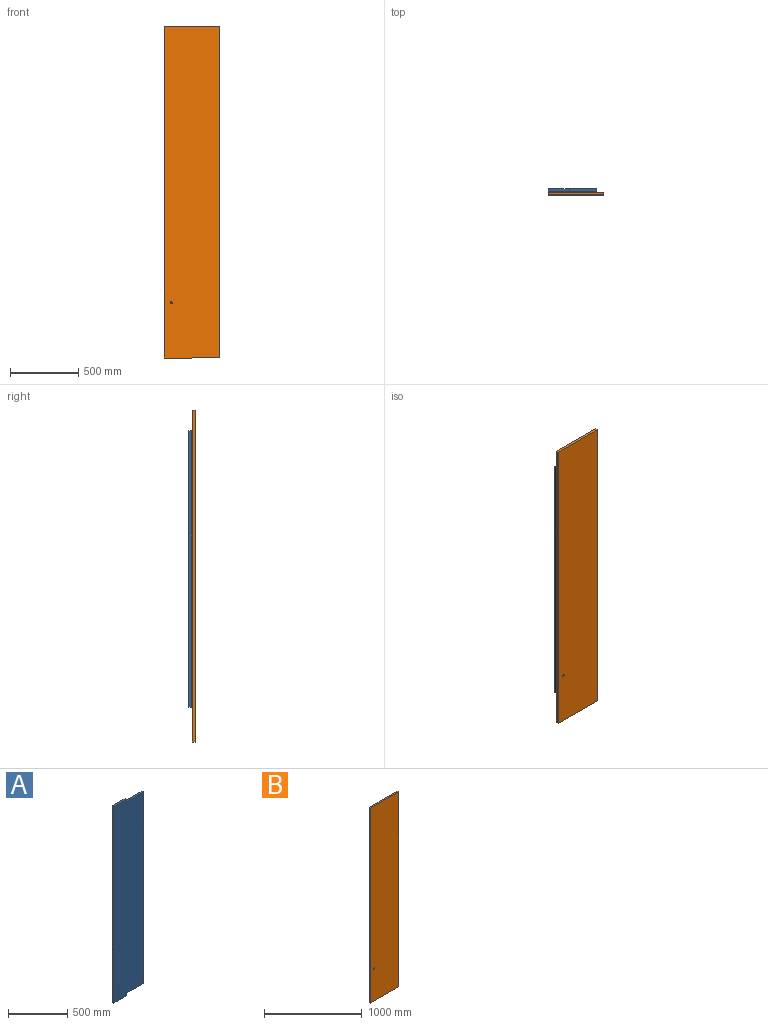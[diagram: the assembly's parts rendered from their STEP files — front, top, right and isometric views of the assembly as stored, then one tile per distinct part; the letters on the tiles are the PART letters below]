
ASSEMBLY  parts=2 mates=1
PART A: 11 faces, bbox 355.6x19.1x2032 mm
  f0: plane 26.04x19.05mm, normal (1,0,0), area 496mm2, adj f1,f7,f9,f10
  f1: plane 203.2x19.05mm, normal (0,0,-1), area 3871mm2, adj f0,f2,f9,f10
  f2: plane 1981.2x19.05mm, normal (1,0,0), area 37741.9mm2, adj f1,f3,f9,f10
  f3: plane 203.2x19.05mm, normal (0,0,1), area 3871mm2, adj f2,f4,f9,f10
  f4: plane 24.76x19.05mm, normal (1,0,0), area 471.8mm2, adj f3,f5,f9,f10
  f5: plane 152.4x19.05mm, normal (0,0,1), area 2903.2mm2, adj f4,f6,f9,f10
  f6: plane 2032x19.05mm, normal (-1,0,0), area 38709.6mm2, adj f5,f7,f9,f10
  f7: plane 152.4x19.05mm, normal (0,0,-1), area 2903.2mm2, adj f0,f6,f9,f10
  f8: cylinder r=6.35mm len=19.05mm, axis (0,-1,0), area 760.1mm2, adj f9,f10
  f9: plane 2032x355.6mm, normal (0,1,0), area 712130mm2, adj f0,f1,f2,f3,f4,f5,f6,f7
  f10: plane 2032x355.6mm, normal (0,-1,0), area 712130mm2, adj f0,f1,f2,f3,f4,f5,f6,f7
PART B: 7 faces, bbox 406.4x19.1x2438.4 mm
  f0: plane 406.4x19.05mm, normal (0,0,1), area 7741.9mm2, adj f1,f4,f5,f6
  f1: plane 2438.4x19.05mm, normal (-1,0,0), area 46451.5mm2, adj f0,f2,f5,f6
  f2: plane 406.4x19.05mm, normal (0,0,-1), area 7741.9mm2, adj f1,f4,f5,f6
  f3: cylinder r=6.35mm len=19.05mm, axis (0,1,0), area 760.1mm2, adj f5,f6
  f4: plane 2438.4x19.05mm, normal (1,0,0), area 46451.5mm2, adj f0,f2,f5,f6
  f5: plane 2438.4x406.4mm, normal (0,-1,0), area 990839.1mm2, adj f0,f1,f2,f3,f4
  f6: plane 2438.4x406.4mm, normal (0,1,0), area 990839.1mm2, adj f0,f1,f2,f3,f4
PLACE A rot(axis=(0,1,0),0deg) t=(2472.84,0,1059.76)mm
PLACE B rot(axis=(-0.01,-0.95,-0.31),0deg) t=(2542.76,-6.35,1297.52)mm
MATE revolute B.f3 <-> A.f8  axis (0,1,0) through (2355.22,-15.88,1163.52)mm
